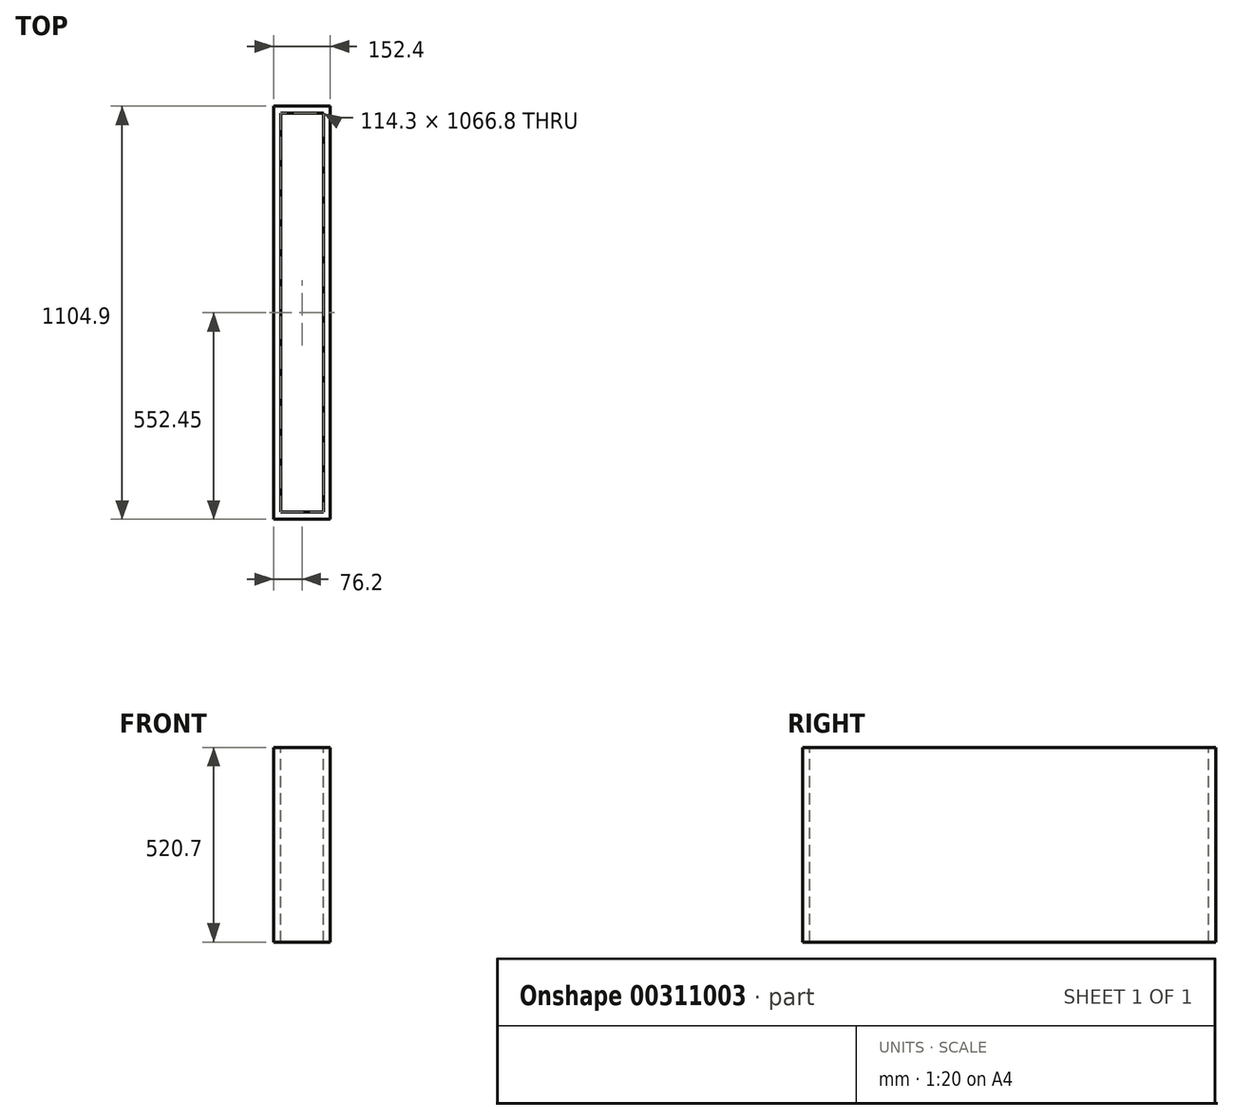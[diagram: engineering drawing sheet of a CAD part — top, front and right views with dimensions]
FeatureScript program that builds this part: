
annotation { "Feature Type Name" : "Feature", "Feature Type Description" : "" }
export const myFeature = defineFeature(function(context is Context, id is Id, definition is map)
    precondition{}
    {
        {
            var Q0;
            Q0=qCreatedBy(makeId("Front.planeOp"),FACE);
            var sketch = newSketch(context, id + "F0", { "sketchPlane" : qUnion([Q0])});
            skLineSegment(sketch, "E0", {"start": v(0, 0) * mm, "end": v(152.4, 0) * mm});
            skLineSegment(sketch, "E1", {"start": v(152.4, 0) * mm, "end": v(152.4, -520.7) * mm});
            skLineSegment(sketch, "E2", {"start": v(152.4, -520.7) * mm, "end": v(0, -520.7) * mm});
            skLineSegment(sketch, "E3", {"start": v(0, -520.7) * mm, "end": v(0, 0) * mm});
            skSolve(sketch);
        }
        {
            var Q0;
            Q0=makeQuery(id+"F0.imprint","IMPRINT",FACE,{"disambiguationData":[TD([[makeQuery(id+"F0.imprint","IMPRINT",EDGE,{"derivedFrom":sQuery(id+"F0.wireOp",EDGE,"E0")}),-1.0]])]});
            extrude(context, id + "F1", {"entities" : qUnion([Q0]), "oppositeDirection" : true, "depth" : 1104.9 * mm});
        }
        {
            var Q0;
            Q0=makeQuery(id+"F1.opExtrude","SWEPT_FACE",FACE,{"disambiguationData":[OSD([sQuery(id+"F0.wireOp",EDGE,"E0")])]});
            var sketch = newSketch(context, id + "F2", { "sketchPlane" : qUnion([Q0])});
            skLineSegment(sketch, "E4.bottom", {"start": v(19.05, 1085.85) * mm, "end": v(133.35, 1085.85) * mm});
            skLineSegment(sketch, "E4.top", {"start": v(19.05, 19.05) * mm, "end": v(133.35, 19.05) * mm});
            skLineSegment(sketch, "E4.left", {"start": v(19.05, 1085.85) * mm, "end": v(19.05, 19.05) * mm});
            skLineSegment(sketch, "E4.right", {"start": v(133.35, 1085.85) * mm, "end": v(133.35, 19.05) * mm});
            skSolve(sketch);
        }
        {
            var Q0;
            Q0=makeQuery(id+"F2.imprint","IMPRINT",FACE,{"disambiguationData":[TD([[makeQuery(id+"F2.imprint","IMPRINT",EDGE,{"derivedFrom":sQuery(id+"F2.wireOp",EDGE,"E4.bottom")}),-1.0]])]});
            extrude(context, id + "F3", {"entities" : qUnion([Q0]), "operationType" : NewBodyOperationType.REMOVE, "endBound" : BoundingType.THROUGH_ALL, "oppositeDirection" : true, "depth" : 25.4 * mm});
        }
    });
